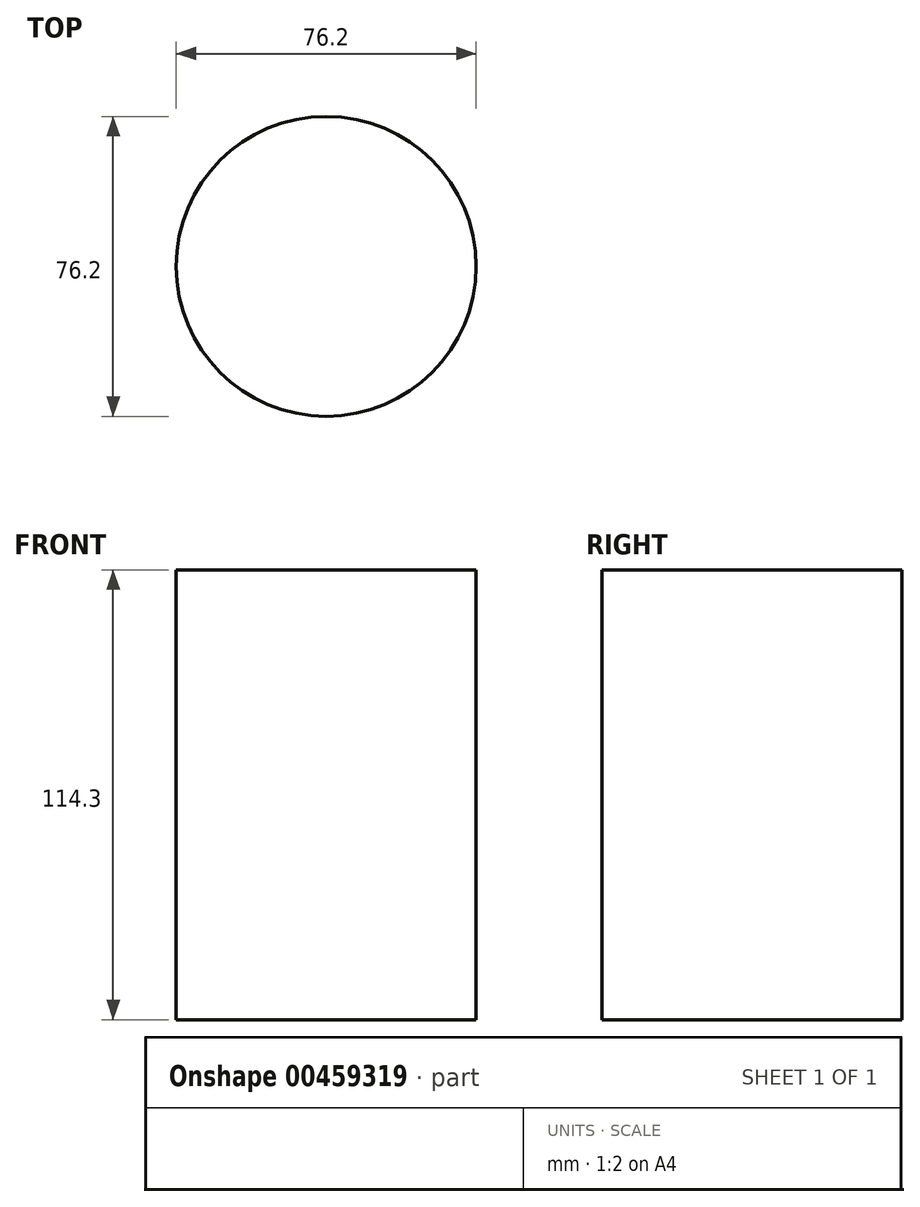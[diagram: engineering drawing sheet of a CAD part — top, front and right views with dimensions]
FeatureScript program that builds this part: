
annotation { "Feature Type Name" : "Feature", "Feature Type Description" : "" }
export const myFeature = defineFeature(function(context is Context, id is Id, definition is map)
    precondition{}
    {
        {
            var Q0;
            Q0=qCreatedBy(makeId("Top.planeOp"),FACE);
            var sketch = newSketch(context, id + "F0", { "sketchPlane" : qUnion([Q0])});
            skCircle(sketch, "E0", {"center": v(0, 0) * mm, "radius": 38.1 * mm});
            skSolve(sketch);
        }
        {
            var Q0;
            Q0 = qSketchRegion(id + "F0", true);
            extrude(context, id + "F1", {"entities" : qUnion([Q0]), "depth" : 114.3 * mm});
        }
    });
